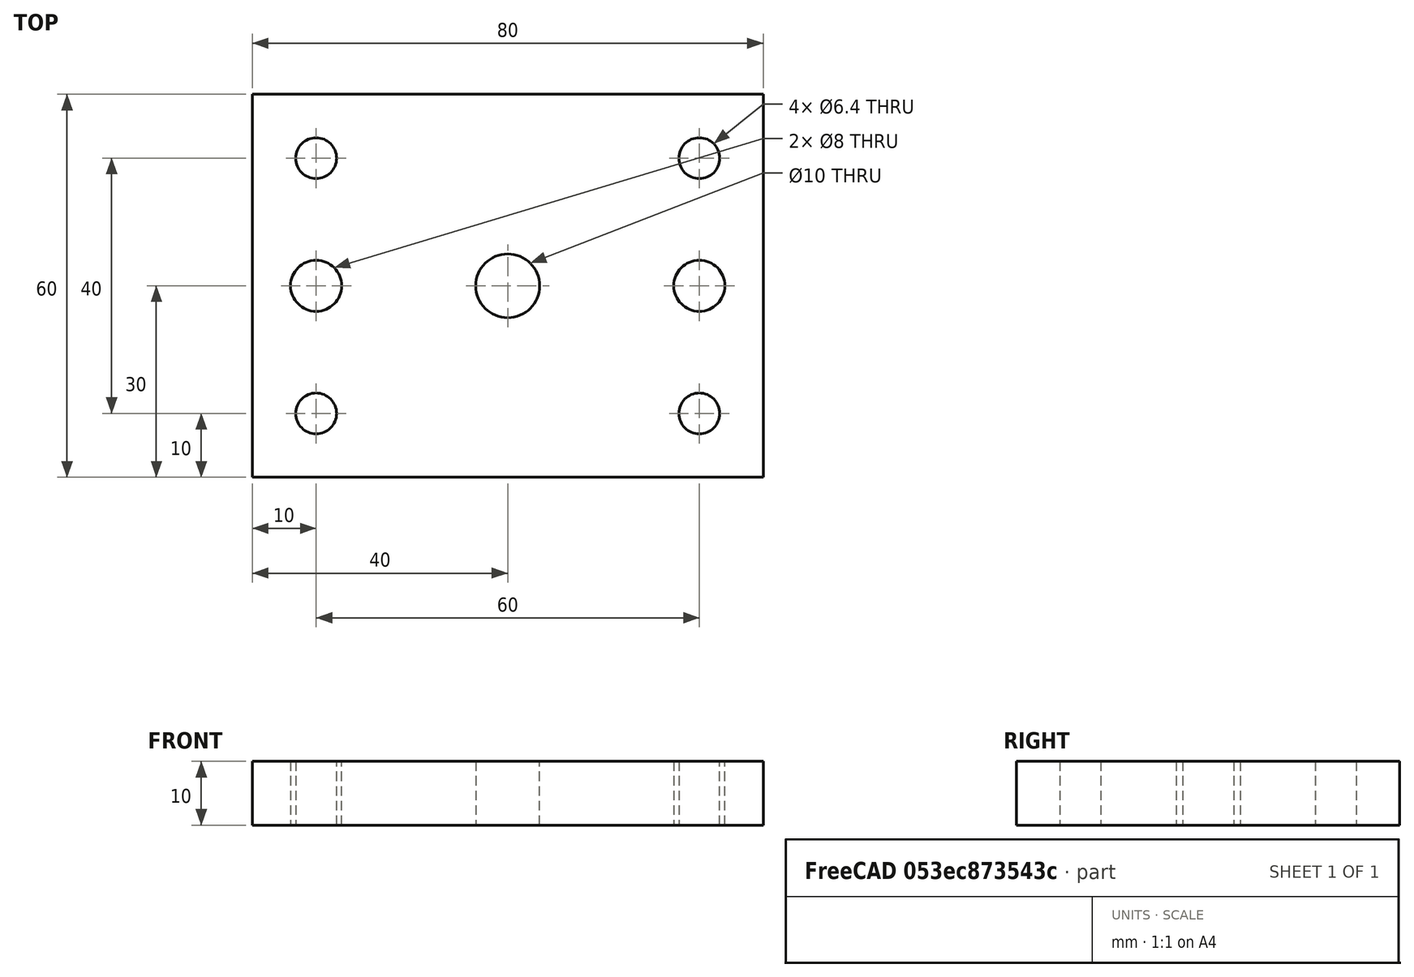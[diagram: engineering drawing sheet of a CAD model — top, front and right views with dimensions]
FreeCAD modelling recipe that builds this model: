
FCSTD DOCUMENT  (FreeCAD 0.18R16110 (Git))
Label: mountplate1c_festlager
License: All rights reserved
LicenseURL: http://en.wikipedia.org/wiki/All_rights_reserved
objects: Sketcher::SketchObject×1, PartDesign::Pad×1, PartDesign::Body×1
note: 4 computed .brp shape members not serialized (recipe doc carries the construction recipe); baked Part::Feature solids carry a one-line shape summary decoded from their .brp

FEATURE [Sketcher::SketchObject] Sketch
  MapMode = 5
  Support = -> [XY_Plane]
  sketch-geometry (11):
    g0: LineSegment StartX=0 StartY=60 StartZ=0 EndX=80 EndY=60 EndZ=0
    g1: LineSegment StartX=80 StartY=60 StartZ=0 EndX=80 EndY=0 EndZ=0
    g2: LineSegment StartX=80 StartY=0 StartZ=0 EndX=0 EndY=0 EndZ=0
    g3: LineSegment StartX=0 StartY=0 StartZ=0 EndX=0 EndY=60 EndZ=0
    g4: Circle CenterX=40 CenterY=30 CenterZ=0 NormalX=0 NormalY=0 NormalZ=1 AngleXU=0 Radius=5
    g5: Circle CenterX=10 CenterY=10 CenterZ=0 NormalX=0 NormalY=0 NormalZ=1 AngleXU=0 Radius=3.2
    g6: Circle CenterX=70 CenterY=10 CenterZ=0 NormalX=0 NormalY=0 NormalZ=1 AngleXU=0 Radius=3.2
    g7: Circle CenterX=70 CenterY=30 CenterZ=0 NormalX=0 NormalY=0 NormalZ=1 AngleXU=0 Radius=4
    g8: Circle CenterX=10 CenterY=30 CenterZ=0 NormalX=0 NormalY=0 NormalZ=1 AngleXU=0 Radius=4
    g9: Circle CenterX=10 CenterY=50 CenterZ=0 NormalX=0 NormalY=0 NormalZ=1 AngleXU=0 Radius=3.2
    g10: Circle CenterX=70 CenterY=50 CenterZ=0 NormalX=0 NormalY=0 NormalZ=1 AngleXU=0 Radius=3.2
  constraints (32):
    c: Coincident(g0,g1)
    c: Coincident(g1,g2)
    c: Coincident(g2,g3)
    c: Coincident(g3,g0)
    c: Horizontal(g0)
    c: Horizontal(g2)
    c: Vertical(g1)
    c: Vertical(g3)
    c: Coincident(g2,g-1)
    c: DistanceY(g3,g3) = 60
    c: DistanceX(g2,g2) = 80
    c: DistanceX(g2,g4) = 40
    c: DistanceY(g2,g4) = 30
    c: Radius(g4) = 5
    c: DistanceX(g2,g5) = 10
    c: DistanceY(g2,g5) = 10
    c: DistanceY(g5,g6) = 0
    c: DistanceX(g6,g1) = 10
    c: DistanceX(g8,g5) = 0
    c: DistanceY(g7,g8) = 0
    c: DistanceX(g7,g0) = 10
    c: DistanceY(g8,g0) = 30
    c: Radius(g5) = 3.2
    c: Equal(g5,g6)
    c: Radius(g8) = 4
    c: Equal(g8,g7)
    c: DistanceX(g7,g10) = 0
    c: DistanceX(g9,g8) = 0
    c: DistanceY(g9,g0) = 10
    c: DistanceY(g10,g0) = 10
    c: Radius(g10) = 3.2
    c: Radius(g9) = 3.2
FEATURE [PartDesign::Pad] Pad
  Length = 10
  Length2 = 100
  Profile = -> Sketch
  Type = 0
FEATURE [PartDesign::Body] Body
  Group = -> [Sketch,Pad]
  Origin = -> Origin
  Tip = -> Pad
